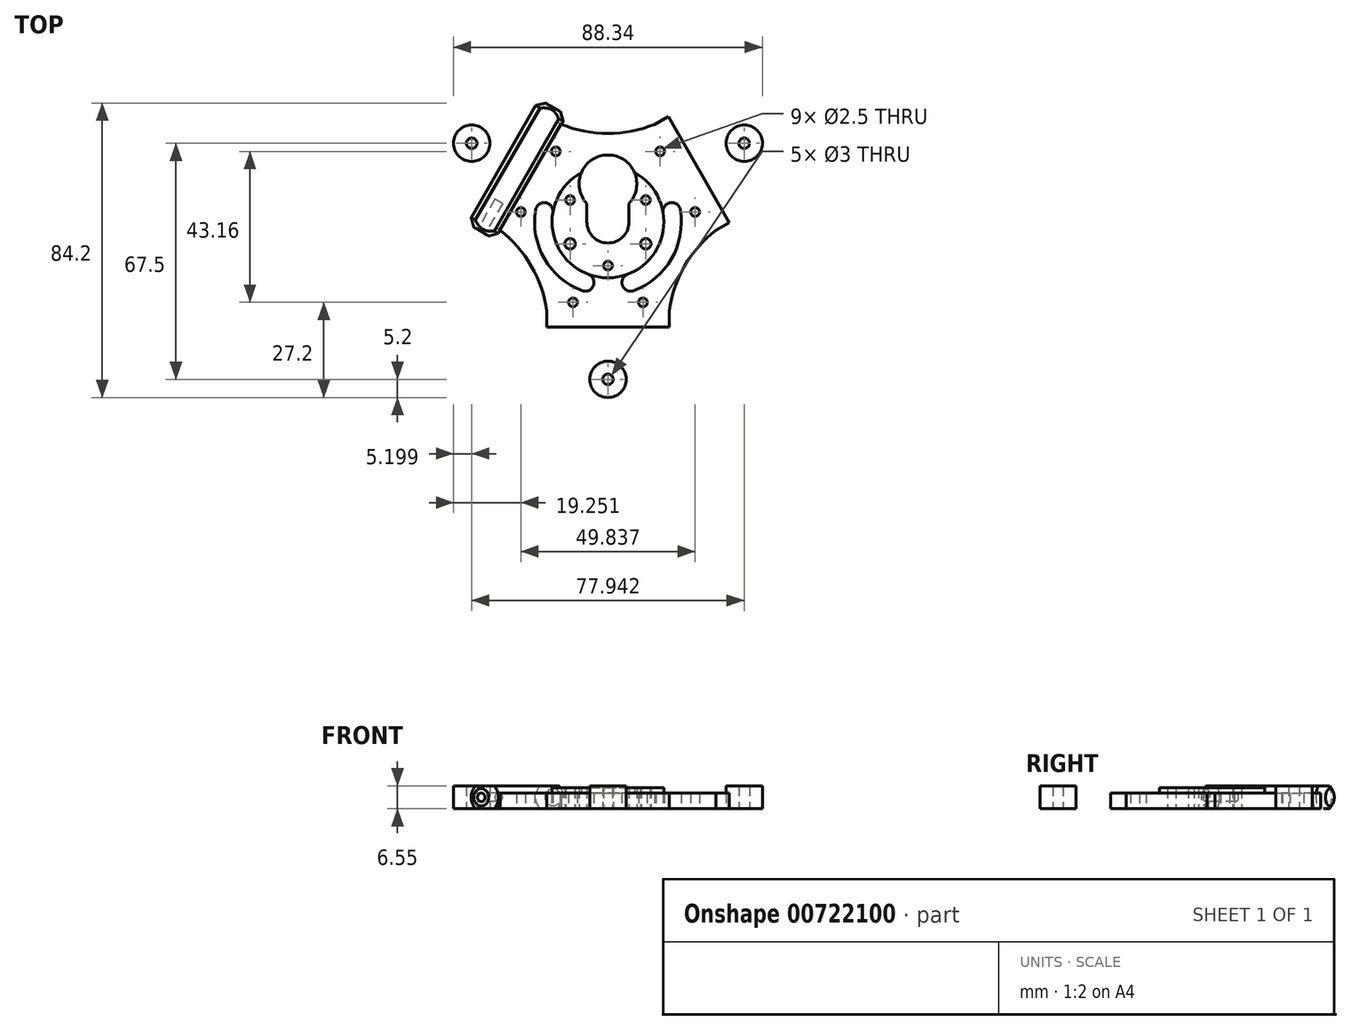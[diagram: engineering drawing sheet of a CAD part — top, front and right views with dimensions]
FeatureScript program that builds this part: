
annotation { "Feature Type Name" : "Feature", "Feature Type Description" : "" }
export const myFeature = defineFeature(function(context is Context, id is Id, definition is map)
    precondition{}
    {
        {
            var Q0;
            Q0=qCreatedBy(makeId("Top.planeOp"),FACE);
            var sketch = newSketch(context, id + "F0", { "sketchPlane" : qUnion([Q0])});
            skArc(sketch, "E0", {"start": v(-6.03, 0) * mm, "mid": v(0, -6.03) * mm, "end": v(6.03, 0) * mm});
            skArc(sketch, "E1", {"start": v(6.03, 5.26) * mm, "mid": v(0, 19.15) * mm, "end": v(-6.03, 5.26) * mm});
            skLineSegment(sketch, "E2", {"start": v(6.03, 0) * mm, "end": v(6.03, 5.26) * mm});
            skLineSegment(sketch, "E3", {"start": v(-6.03, 0) * mm, "end": v(-6.03, 5.26) * mm});
            skLineSegment(sketch, "E4", {"start": v(-32.33, -5) * mm, "end": v(-30.83, -2.4) * mm, "construction": true});
            skLineSegment(sketch, "E5", {"start": v(-11.83, 30.5) * mm, "end": v(-19.63, 35) * mm, "construction": true});
            skLineSegment(sketch, "E6", {"start": v(-19.63, 35) * mm, "end": v(-40.13, -0.5) * mm, "construction": true});
            skLineSegment(sketch, "E7", {"start": v(-40.13, -0.5) * mm, "end": v(-32.33, -5) * mm, "construction": true});
            skLineSegment(sketch, "E8", {"start": v(-36.23, -2.75) * mm, "end": v(-34.73, -0.16) * mm, "construction": true});
            skLineSegment(sketch, "E9", {"start": v(-25.98, 15) * mm, "end": v(0, 0) * mm, "construction": true});
            skCircle(sketch, "E10", {"center": v(0, 0) * mm, "radius": 8 * mm, "construction": true});
            skLineSegment(sketch, "E11.1.0", {"start": v(20.5, -25.5) * mm, "end": v(17.5, -25.5) * mm, "construction": true});
            skLineSegment(sketch, "E11.1.1", {"start": v(-20.5, -25.5) * mm, "end": v(-20.5, -34.5) * mm, "construction": true});
            skLineSegment(sketch, "E11.1.2", {"start": v(-20.5, -34.5) * mm, "end": v(20.5, -34.5) * mm, "construction": true});
            skLineSegment(sketch, "E11.1.3", {"start": v(20.5, -34.5) * mm, "end": v(20.5, -25.5) * mm, "construction": true});
            skLineSegment(sketch, "E11.1.4", {"start": v(0, -30) * mm, "end": v(0, 0) * mm, "construction": true});
            skLineSegment(sketch, "E11.1.5", {"start": v(20.5, -30) * mm, "end": v(-20.5, -30) * mm, "construction": true});
            skLineSegment(sketch, "E11.2.0", {"start": v(11.83, 30.5) * mm, "end": v(13.33, 27.9) * mm, "construction": true});
            skLineSegment(sketch, "E11.2.1", {"start": v(32.33, -5) * mm, "end": v(40.13, -0.5) * mm, "construction": true});
            skLineSegment(sketch, "E11.2.2", {"start": v(40.13, -0.5) * mm, "end": v(19.63, 35) * mm, "construction": true});
            skLineSegment(sketch, "E11.2.3", {"start": v(19.63, 35) * mm, "end": v(11.83, 30.5) * mm, "construction": true});
            skLineSegment(sketch, "E11.2.4", {"start": v(25.98, 15) * mm, "end": v(0, 0) * mm, "construction": true});
            skLineSegment(sketch, "E11.2.5", {"start": v(15.73, 32.75) * mm, "end": v(36.23, -2.75) * mm, "construction": true});
            skArc(sketch, "E12", {"start": v(-13.33, 27.9) * mm, "mid": v(0, 25.3) * mm, "end": v(13.33, 27.9) * mm});
            skArc(sketch, "E13.1.0", {"start": v(-17.5, -25.5) * mm, "mid": v(-21.92, -12.65) * mm, "end": v(-30.83, -2.4) * mm});
            skArc(sketch, "E13.2.0", {"start": v(30.83, -2.4) * mm, "mid": v(21.92, -12.65) * mm, "end": v(17.5, -25.5) * mm});
            skLineSegment(sketch, "E14.trimOffspring", {"start": v(-13.33, 27.9) * mm, "end": v(-11.83, 30.5) * mm, "construction": true});
            skLineSegment(sketch, "E15.trimOffspring", {"start": v(-17.5, -25.5) * mm, "end": v(-20.5, -25.5) * mm, "construction": true});
            skLineSegment(sketch, "E16.trimOffspring", {"start": v(30.83, -2.4) * mm, "end": v(32.33, -5) * mm, "construction": true});
            skCircle(sketch, "E17", {"center": v(0, -12.5) * mm, "radius": 1.25 * mm});
            skCircle(sketch, "E18.2.0", {"center": v(10.83, 6.25) * mm, "radius": 1.25 * mm});
            skCircle(sketch, "E18.4.0", {"center": v(-10.83, 6.25) * mm, "radius": 1.25 * mm});
            skCircle(sketch, "E18.5.0", {"center": v(-10.83, -6.25) * mm, "radius": 1.5 * mm});
            skCircle(sketch, "E19", {"center": v(-24.92, 2.84) * mm, "radius": 1.25 * mm});
            skCircle(sketch, "E20.MirrorC", {"center": v(-14.92, 20.16) * mm, "radius": 1.25 * mm});
            skArc(sketch, "E21", {"start": v(-15.78, 2.62) * mm, "mid": v(-13.86, -8) * mm, "end": v(-5.62, -14.98) * mm});
            skCircle(sketch, "E22.1.0", {"center": v(10, -23) * mm, "radius": 1.25 * mm});
            skCircle(sketch, "E22.1.1", {"center": v(-10, -23) * mm, "radius": 1.25 * mm});
            skCircle(sketch, "E22.2.0", {"center": v(14.92, 20.16) * mm, "radius": 1.25 * mm});
            skCircle(sketch, "E22.2.1", {"center": v(24.92, 2.84) * mm, "radius": 1.25 * mm});
            skArc(sketch, "E23", {"start": v(-20.72, 3.44) * mm, "mid": v(-18.19, -10.5) * mm, "end": v(-7.38, -19.66) * mm});
            skArc(sketch, "E24", {"start": v(-15.78, 2.62) * mm, "mid": v(-17.84, 5.5) * mm, "end": v(-20.72, 3.44) * mm});
            skArc(sketch, "E25", {"start": v(-7.38, -19.66) * mm, "mid": v(-4.16, -18.2) * mm, "end": v(-5.62, -14.98) * mm});
            skArc(sketch, "E26.MirrorCS", {"start": v(15.78, 2.62) * mm, "mid": v(13.86, -8) * mm, "end": v(5.62, -14.98) * mm});
            skArc(sketch, "E27.MirrorCS", {"start": v(20.72, 3.44) * mm, "mid": v(18.19, -10.5) * mm, "end": v(7.38, -19.66) * mm});
            skArc(sketch, "E28.MirrorCS", {"start": v(15.78, 2.62) * mm, "mid": v(17.84, 5.5) * mm, "end": v(20.72, 3.44) * mm});
            skArc(sketch, "E29.MirrorCS", {"start": v(7.38, -19.66) * mm, "mid": v(4.16, -18.2) * mm, "end": v(5.62, -14.98) * mm});
            skLineSegment(sketch, "E30", {"start": v(-10.83, -6.25) * mm, "end": v(0, 0) * mm, "construction": true});
            skCircle(sketch, "E31", {"center": v(0, 0) * mm, "radius": 12.5 * mm, "construction": true});
            skCircle(sketch, "E32.MirrorC", {"center": v(10.83, -6.25) * mm, "radius": 1.5 * mm});
            skLineSegment(sketch, "E33", {"start": v(-13.33, 27.9) * mm, "end": v(-17.23, 30.16) * mm});
            skLineSegment(sketch, "E34", {"start": v(-17.23, 30.16) * mm, "end": v(-34.73, -0.16) * mm});
            skLineSegment(sketch, "E35", {"start": v(-34.73, -0.16) * mm, "end": v(-30.83, -2.4) * mm});
            skLineSegment(sketch, "E36.trimOffspring", {"start": v(-17.23, 30.16) * mm, "end": v(-15.73, 32.75) * mm, "construction": true});
            skLineSegment(sketch, "E37.1.0", {"start": v(-17.5, -25.5) * mm, "end": v(-17.5, -30) * mm});
            skLineSegment(sketch, "E37.1.1", {"start": v(-17.5, -30) * mm, "end": v(17.5, -30) * mm});
            skLineSegment(sketch, "E37.1.2", {"start": v(17.5, -30) * mm, "end": v(17.5, -25.5) * mm});
            skLineSegment(sketch, "E37.2.0", {"start": v(30.83, -2.4) * mm, "end": v(34.73, -0.16) * mm});
            skLineSegment(sketch, "E37.2.1", {"start": v(34.73, -0.16) * mm, "end": v(17.23, 30.16) * mm});
            skLineSegment(sketch, "E37.2.2", {"start": v(17.23, 30.16) * mm, "end": v(13.33, 27.9) * mm});
            skSolve(sketch);
        }
        {
            var Q0;
            Q0=qSketchRegion(id+"F0",true);
            extrude(context, id + "F1", {"entities" : qUnion([Q0]), "depth" : 4.5 * mm, "offsetDistance" : 25 * mm});
        }
        {
            var Q0;
            Q0=qCreatedBy(makeId("Front.planeOp"),FACE);
            var sketch = newSketch(context, id + "F2", { "sketchPlane" : qUnion([Q0])});
            skLineSegment(sketch, "E38", {"start": v(0, 0) * mm, "end": v(0, 59.84) * mm, "construction": true});
            skSolve(sketch);
        }
        {
            var Q0;
            {var subQ0=sQuery(id+"F0.wireOp",EDGE,"E29.MirrorCS");var subQ2=sQuery(id+"F0.wireOp",EDGE,"E28.MirrorCS");var subQ4=sQuery(id+"F0.wireOp",EDGE,"E27.MirrorCS");var subQ8=sQuery(id+"F0.wireOp",EDGE,"E26.MirrorCS");var subQ11=sQuery(id+"F0.wireOp",EDGE,"E25");var subQ14=sQuery(id+"F0.wireOp",EDGE,"E24");var subQ16=sQuery(id+"F0.wireOp",EDGE,"E23");var subQ18=sQuery(id+"F0.wireOp",EDGE,"E22.2.1");var subQ20=sQuery(id+"F0.wireOp",EDGE,"E22.2.0");var subQ22=sQuery(id+"F0.wireOp",EDGE,"E22.1.1");var subQ24=sQuery(id+"F0.wireOp",EDGE,"E22.1.0");var subQ26=sQuery(id+"F0.wireOp",EDGE,"E21");var subQ28=sQuery(id+"F0.wireOp",EDGE,"E20.MirrorC");var subQ30=sQuery(id+"F0.wireOp",EDGE,"E19");var subQ32=sQuery(id+"F0.wireOp",EDGE,"E18.5.0");var subQ34=sQuery(id+"F0.wireOp",EDGE,"E18.4.0");var subQ36=sQuery(id+"F0.wireOp",EDGE,"E11.1.3");var subQ38=sQuery(id+"F0.wireOp",EDGE,"E11.1.0");var subQ40=sQuery(id+"F0.wireOp",EDGE,"E7");var subQ42=sQuery(id+"F0.wireOp",EDGE,"E5");var subQ47=sQuery(id+"F0.wireOp",EDGE,"E17");var subQ49=sQuery(id+"F0.wireOp",EDGE,"E4");var subQ51=sQuery(id+"F0.wireOp",EDGE,"E11.1.1");var subQ53=sQuery(id+"F0.wireOp",EDGE,"E0");var subQ54=makeQuery(id+"F1.opExtrude","SWEPT_FACE",FACE,{"disambiguationData":[OSD([subQ53])]});var subQ55=sQuery(id+"F0.wireOp",EDGE,"E16.trimOffspring");var subQ57=sQuery(id+"F0.wireOp",EDGE,"E3");var subQ59=sQuery(id+"F0.wireOp",EDGE,"E1");var subQ61=sQuery(id+"F0.wireOp",EDGE,"E18.2.0");var subQ63=sQuery(id+"F0.wireOp",EDGE,"E2");var subQ65=sQuery(id+"F0.wireOp",EDGE,"E11.2.0");var subQ67=sQuery(id+"F0.wireOp",EDGE,"E11.2.1");var subQ69=sQuery(id+"F0.wireOp",EDGE,"E11.2.3");var subQ72=sQuery(id+"F0.wireOp",EDGE,"E12");var subQ74=sQuery(id+"F0.wireOp",EDGE,"E13.1.0");var subQ76=sQuery(id+"F0.wireOp",EDGE,"E13.2.0");var subQ78=sQuery(id+"F0.wireOp",EDGE,"E14.trimOffspring");var subQ80=sQuery(id+"F0.wireOp",EDGE,"E15.trimOffspring");var subQ82=sQuery(id+"F0.wireOp",EDGE,"E18.1.0");var subQ84=sQuery(id+"F0.wireOp",EDGE,"E11.2.2");var subQ86=sQuery(id+"F0.wireOp",EDGE,"E11.1.2");Q0=makeQuery(id+"Fxi4iVRiwFdOaLl_1.2.FuNoGRhF2MTlrvA_1.boolean.opBoolean","SPLIT",FACE,{"disambiguationData":[TD([subQ54])],"derivedFrom":makeQuery(id+"Fxi4iVRiwFdOaLl_1.1.FuNoGRhF2MTlrvA_1.boolean.opBoolean","SPLIT",FACE,{"disambiguationData":[TD([subQ54])],"derivedFrom":makeQuery(id+"FuNoGRhF2MTlrvA_1.boolean.opBoolean","SPLIT",FACE,{"disambiguationData":[TD([subQ54])],"derivedFrom":makeQuery(id+"F1.opExtrude","CAP_FACE",FACE,{"disambiguationData":[OSD([subQ53,subQ59,subQ63,subQ57,subQ49,subQ42,sQuery(id+"F0.wireOp",EDGE,"E6"),subQ40,subQ38,subQ51,subQ86,subQ36,subQ65,subQ67,subQ84,subQ69,subQ72,subQ74,subQ76,subQ78,subQ80,subQ55,subQ47,subQ82,subQ61,subQ34,subQ32,subQ30,subQ28,subQ26,subQ24,subQ22,subQ20,subQ18,subQ16,subQ14,subQ11,subQ8,subQ4,subQ2,subQ0])],"isStart":false})})})});}
            var sketch = newSketch(context, id + "F3", { "sketchPlane" : qUnion([Q0])});
            skArc(sketch, "E39", {"start": v(-7.62, 14.07) * mm, "mid": v(0, -16) * mm, "end": v(7.62, 14.07) * mm});
            skArc(sketch, "E40.0", {"start": v(6.03, 5.26) * mm, "mid": v(8.12, 9.43) * mm, "end": v(7.62, 14.07) * mm});
            skLineSegment(sketch, "E41.0", {"start": v(-6.03, 0) * mm, "end": v(-6.03, 5.26) * mm});
            skArc(sketch, "E42.0", {"start": v(-6.03, 0) * mm, "mid": v(0, -6.03) * mm, "end": v(6.03, 0) * mm});
            skLineSegment(sketch, "E43.0", {"start": v(6.03, 0) * mm, "end": v(6.03, 5.26) * mm});
            skCircle(sketch, "E44.0", {"center": v(10.83, 6.25) * mm, "radius": 1.25 * mm});
            skCircle(sketch, "E45.0", {"center": v(0, -12.5) * mm, "radius": 1.25 * mm});
            skCircle(sketch, "E46.0", {"center": v(-10.83, -6.25) * mm, "radius": 1.5 * mm});
            skCircle(sketch, "E47.0", {"center": v(-10.83, 6.25) * mm, "radius": 1.25 * mm});
            skArc(sketch, "E48.trimOffspring", {"start": v(-7.62, 14.07) * mm, "mid": v(-8.12, 9.43) * mm, "end": v(-6.03, 5.26) * mm});
            skCircle(sketch, "E49.0", {"center": v(10.83, -6.25) * mm, "radius": 1.5 * mm});
            skSolve(sketch);
        }
        {
            var Q0;
            Q0=qSketchRegion(id+"F3",true);
            var Q1;
            Q1=makeQuery(id+"F1.opExtrude","CAP_FACE",FACE,{"disambiguationData":[OSD([sQuery(id+"F0.wireOp",EDGE,"E0"),sQuery(id+"F0.wireOp",EDGE,"E1"),sQuery(id+"F0.wireOp",EDGE,"E2"),sQuery(id+"F0.wireOp",EDGE,"E3"),sQuery(id+"F0.wireOp",EDGE,"E4"),sQuery(id+"F0.wireOp",EDGE,"E5"),sQuery(id+"F0.wireOp",EDGE,"E6"),sQuery(id+"F0.wireOp",EDGE,"E7"),sQuery(id+"F0.wireOp",EDGE,"E11.1.0"),sQuery(id+"F0.wireOp",EDGE,"E11.1.1"),sQuery(id+"F0.wireOp",EDGE,"E11.1.2"),sQuery(id+"F0.wireOp",EDGE,"E11.1.3"),sQuery(id+"F0.wireOp",EDGE,"E11.2.0"),sQuery(id+"F0.wireOp",EDGE,"E11.2.1"),sQuery(id+"F0.wireOp",EDGE,"E11.2.2"),sQuery(id+"F0.wireOp",EDGE,"E11.2.3"),sQuery(id+"F0.wireOp",EDGE,"E12"),sQuery(id+"F0.wireOp",EDGE,"E13.1.0"),sQuery(id+"F0.wireOp",EDGE,"E13.2.0"),sQuery(id+"F0.wireOp",EDGE,"E14.trimOffspring"),sQuery(id+"F0.wireOp",EDGE,"E15.trimOffspring"),sQuery(id+"F0.wireOp",EDGE,"E16.trimOffspring"),sQuery(id+"F0.wireOp",EDGE,"E17"),sQuery(id+"F0.wireOp",EDGE,"E18.1.0"),sQuery(id+"F0.wireOp",EDGE,"E18.2.0"),sQuery(id+"F0.wireOp",EDGE,"E18.4.0"),sQuery(id+"F0.wireOp",EDGE,"E18.5.0"),sQuery(id+"F0.wireOp",EDGE,"E19"),sQuery(id+"F0.wireOp",EDGE,"E20.MirrorC"),sQuery(id+"F0.wireOp",EDGE,"E21"),sQuery(id+"F0.wireOp",EDGE,"E22.1.0"),sQuery(id+"F0.wireOp",EDGE,"E22.1.1"),sQuery(id+"F0.wireOp",EDGE,"E22.2.0"),sQuery(id+"F0.wireOp",EDGE,"E22.2.1"),sQuery(id+"F0.wireOp",EDGE,"E23"),sQuery(id+"F0.wireOp",EDGE,"E24"),sQuery(id+"F0.wireOp",EDGE,"E25"),sQuery(id+"F0.wireOp",EDGE,"E26.MirrorCS"),sQuery(id+"F0.wireOp",EDGE,"E27.MirrorCS"),sQuery(id+"F0.wireOp",EDGE,"E28.MirrorCS"),sQuery(id+"F0.wireOp",EDGE,"E29.MirrorCS")])],"isStart":true});
            extrude(context, id + "F4", {"entities" : qUnion([Q0]), "operationType" : NewBodyOperationType.ADD, "depth" : 1.45 * mm, "endBoundEntityFace" : qUnion([Q1]), "hasOffset" : true, "offsetDistance" : 10 * mm, "offsetOppositeDirection" : true});
        }
        {
            var Q0;
            Q0=qCreatedBy(makeId("Top.planeOp"),FACE);
            cPlane(context, id + "F5", {"entities" : qUnion([Q0]), "cplaneType" : CPlaneType.OFFSET, "offset" : (6.5 / 2) * mm, "width" : 150 * mm, "height" : 150 * mm});
        }
        {
            var Q0;
            Q0=qCreatedBy(id+"F5.planeOp",FACE);
            var sketch = newSketch(context, id + "F6", { "sketchPlane" : qUnion([Q0])});
            skLineSegment(sketch, "E50.0", {"start": v(-17.23, 30.16) * mm, "end": v(-34.73, -0.16) * mm, "construction": true});
            skLineSegment(sketch, "E51", {"start": v(-25.98, 15) * mm, "end": v(-29.88, 17.25) * mm, "construction": true});
            skLineSegment(sketch, "E52", {"start": v(-29.88, 17.25) * mm, "end": v(-20.63, 33.27) * mm});
            skLineSegment(sketch, "E53", {"start": v(-20.63, 33.27) * mm, "end": v(-17.9, 34) * mm});
            skLineSegment(sketch, "E54", {"start": v(-17.9, 34) * mm, "end": v(-15.73, 32.75) * mm});
            skLineSegment(sketch, "E55.MirrorCS", {"start": v(-29.88, 17.25) * mm, "end": v(-39.13, 1.23) * mm});
            skLineSegment(sketch, "E56.MirrorCS", {"start": v(-39.13, 1.23) * mm, "end": v(-38.4, -1.5) * mm});
            skLineSegment(sketch, "E57.MirrorCS", {"start": v(-38.4, -1.5) * mm, "end": v(-36.23, -2.75) * mm});
            skLineSegment(sketch, "E58", {"start": v(-15.73, 32.75) * mm, "end": v(-36.23, -2.75) * mm});
            skSolve(sketch);
        }
        {
            var Q0;
            Q0 = qSketchRegion(id + "F6", true);
            var Q1;
            Q1=sQuery(id+"F6.wireOp",EDGE,"E58");
            revolve(context, id + "F7", {"operationType" : NewBodyOperationType.ADD, "surfaceOperationType" : NewSurfaceOperationType.NEW, "entities" : qUnion([Q0]), "axis" : qUnion([Q1]), "revolveType" : RevolveType.FULL});
        }
        {
            var Q0;
            Q0=makeQuery(id+"F7.opRevolve","SWEPT_FACE",FACE,{"disambiguationData":[OSD([sQuery(id+"F6.wireOp",EDGE,"E57.MirrorCS")])]});
            var sketch = newSketch(context, id + "F8", { "sketchPlane" : qUnion([Q0])});
            skLineSegment(sketch, "E59.bottom", {"start": v(-37.92, 0) * mm, "end": v(-22.71, 0) * mm});
            skLineSegment(sketch, "E59.top", {"start": v(-37.92, -3.74) * mm, "end": v(-22.71, -3.74) * mm});
            skLineSegment(sketch, "E59.left", {"start": v(-37.92, 0) * mm, "end": v(-37.92, -3.74) * mm});
            skLineSegment(sketch, "E59.right", {"start": v(-22.71, 0) * mm, "end": v(-22.71, -3.74) * mm});
            skLineSegment(sketch, "E60.bottom", {"start": v(-37.92, 6.5) * mm, "end": v(-22.79, 6.5) * mm});
            skLineSegment(sketch, "E60.top", {"start": v(-37.92, 11.98) * mm, "end": v(-22.79, 11.98) * mm});
            skLineSegment(sketch, "E60.left", {"start": v(-37.92, 6.5) * mm, "end": v(-37.92, 11.98) * mm});
            skLineSegment(sketch, "E60.right", {"start": v(-22.79, 6.5) * mm, "end": v(-22.79, 11.98) * mm});
            skSolve(sketch);
        }
        {
            var Q0;
            Q0 = qSketchRegion(id + "F8", true);
            extrude(context, id + "F9", {"entities" : qUnion([Q0]), "operationType" : NewBodyOperationType.REMOVE, "endBound" : BoundingType.THROUGH_ALL, "oppositeDirection" : true, "depth" : 25 * mm, "offsetDistance" : 25 * mm});
        }
        {
            var Q0;
            Q0=makeQuery(id+"F7.opRevolve","SWEPT_FACE",FACE,{"disambiguationData":[OSD([sQuery(id+"F6.wireOp",EDGE,"E57.MirrorCS")])]});
            var sketch = newSketch(context, id + "F10", { "sketchPlane" : qUnion([Q0])});
            skCircle(sketch, "E61", {"center": v(-30, 3.25) * mm, "radius": 1.25 * mm});
            skSolve(sketch);
        }
        {
            var Q0;
            Q0 = qSketchRegion(id + "F10", true);
            extrude(context, id + "F11", {"entities" : qUnion([Q0]), "operationType" : NewBodyOperationType.REMOVE, "oppositeDirection" : true, "depth" : 10 * mm, "offsetDistance" : 25 * mm});
        }
        {
            var Q0;
            Q0=makeQuery(id+"F7.opRevolve","SWEPT_FACE",FACE,{"disambiguationData":[OSD([sQuery(id+"F6.wireOp",EDGE,"E57.MirrorCS")])]});
            var Q1;
            Q1=makeQuery(id+"F7.opRevolve","SWEPT_FACE",FACE,{"disambiguationData":[OSD([sQuery(id+"F6.wireOp",EDGE,"E54")])]});
            cPlane(context, id + "F12", {"entities" : qUnion([Q0, Q1]), "cplaneType" : CPlaneType.MID_PLANE, "offset" : 25 * mm, "width" : 150 * mm, "height" : 150 * mm});
        }
        {
            var Q0;
            Q0=qCreatedBy(makeId("Top.planeOp"),FACE);
            var sketch = newSketch(context, id + "F13", { "sketchPlane" : qUnion([Q0])});
            skLineSegment(sketch, "E62", {"start": v(0, 0) * mm, "end": v(-38.97, 22.5) * mm, "construction": true});
            skCircle(sketch, "E63", {"center": v(-38.97, 22.5) * mm, "radius": 5.2 * mm});
            skCircle(sketch, "E64", {"center": v(-38.97, 22.5) * mm, "radius": 1.5 * mm});
            skSolve(sketch);
        }
        {
            var Q0;
            Q0 = qSketchRegion(id + "F13", true);
            extrude(context, id + "F14", {"entities" : qUnion([Q0]), "depth" : 6.55 * mm, "offsetDistance" : 25 * mm});
        }
        {
            var Q0;
            Q0=makeQuery(id+"F14.opExtrude","SWEPT_BODY",BODY,{"disambiguationData":[OSD([sQuery(id+"F13.wireOp",EDGE,"E63"),sQuery(id+"F13.wireOp",EDGE,"E64")])]});
            var Q1;
            Q1=sQuery(id+"F2.wireOp",EDGE,"E38");
            circularPattern(context, id + "F15", {"entities" : qUnion([Q0]), "axis" : qUnion([Q1]), "angle" : 360 * degree, "instanceCount" : 3, "equalSpace" : true});
        }
    });
